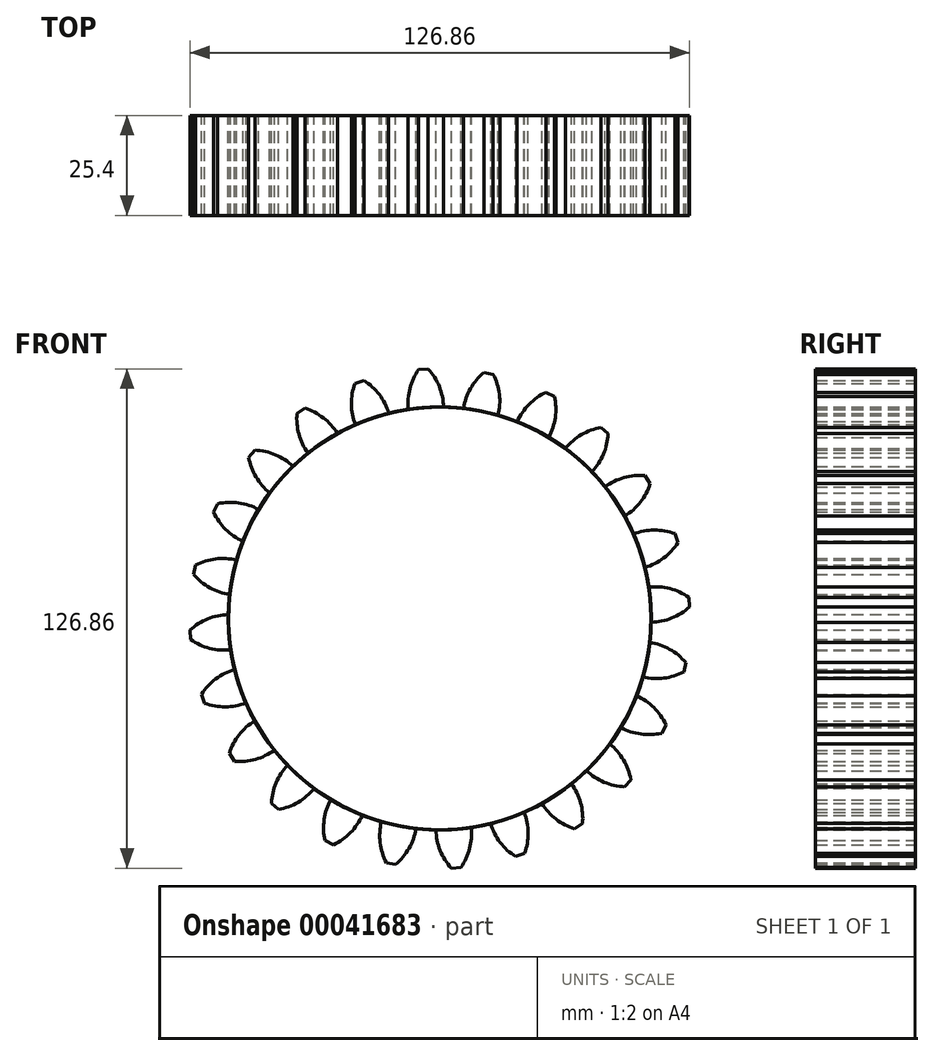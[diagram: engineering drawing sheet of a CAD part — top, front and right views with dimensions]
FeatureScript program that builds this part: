
annotation { "Feature Type Name" : "Feature", "Feature Type Description" : "" }
export const myFeature = defineFeature(function(context is Context, id is Id, definition is map)
    precondition{}
    {
        {
            var Q0;
            Q0=qCreatedBy(makeId("Front.planeOp"),FACE);
            var sketch = newSketch(context, id + "F0", { "sketchPlane" : qUnion([Q0])});
            skCircle(sketch, "E0", {"center": v(0, 0) * mm, "radius": 53.72 * mm});
            skCircle(sketch, "E1", {"center": v(0, 0) * mm, "radius": 58.67 * mm, "construction": true});
            skCircle(sketch, "E2", {"center": v(0, 0) * mm, "radius": 63.5 * mm, "construction": true});
            skLineSegment(sketch, "E3", {"start": v(0, 0) * mm, "end": v(0, 76.8) * mm, "construction": true});
            skLineSegment(sketch, "E4", {"start": v(0, 0) * mm, "end": v(-5.04, 76.92) * mm, "construction": true});
            skLineSegment(sketch, "E5", {"start": v(0, 58.67) * mm, "end": v(-86.24, 58.67) * mm, "construction": true});
            skLineSegment(sketch, "E6", {"start": v(0, 58.67) * mm, "end": v(-90.6, 25.7) * mm, "construction": true});
            skCircle(sketch, "E7", {"center": v(0, 58.67) * mm, "radius": 14.6 * mm, "construction": true});
            skCircle(sketch, "E8", {"center": v(0, 0) * mm, "radius": 55.14 * mm, "construction": true});
            skCircle(sketch, "E9", {"center": v(-13.63, 53.42) * mm, "radius": 14.6 * mm, "construction": true});
            skArc(sketch, "E10", {"start": v(0, 58.63) * mm, "mid": v(0, 58.65) * mm, "end": v(-0.02, 58.67) * mm});
            skPoint(sketch, "E11.orphan", {"position": v(-5.32, 63.28) * mm});
            skPoint(sketch, "E12.MirrorCS.start.orphan", {"position": v(-7.98, 53.13) * mm});
            skPoint(sketch, "E13.orphan", {"position": v(0.97, 53.71) * mm});
            skPoint(sketch, "E14.orphan", {"position": v(-2.99, 63.43) * mm});
            skArc(sketch, "E15", {"start": v(0.97, 53.67) * mm, "mid": v(-0.1, 58.91) * mm, "end": v(-2.96, 63.43) * mm});
            skArc(sketch, "E16.MirrorCS", {"start": v(-7.97, 53.09) * mm, "mid": v(-7.59, 58.42) * mm, "end": v(-5.35, 63.27) * mm});
            skLineSegment(sketch, "E17", {"start": v(-5.35, 63.27) * mm, "end": v(-2.96, 63.43) * mm});
            skSolve(sketch);
        }
        {
            var Q0;
            {var subQ0=sQuery(id+"F0.wireOp",EDGE,"E17");Q0=makeQuery(id+"F0.imprint","IMPRINT",FACE,{"disambiguationData":[TD([[makeQuery(id+"F0.imprint","IMPRINT",EDGE,{"derivedFrom":subQ0}),-1.0]])]});}
            var Q1;
            {var subQ0=sQuery(id+"F0.wireOp",EDGE,"E0");var subQ2=makeQuery(id+"F0.imprint","INTERSECT",VERTEX,{"derivedFrom":[subQ0,sQuery(id+"F0.wireOp",EDGE,"E15")]});Q1=makeQuery(id+"F0.imprint","IMPRINT",FACE,{"disambiguationData":[TD([[makeQuery(id+"F0.imprint","IMPRINT",EDGE,{"disambiguationData":[TD([[subQ2,-1.0]])],"derivedFrom":subQ0}),1.0]])]});}
            extrude(context, id + "F1", {"entities" : qUnion([Q0, Q1]), "depth" : 25.4 * mm});
        }
        {
            var Q0;
            Q0=makeQuery(id+"F1.opExtrude","SWEPT_BODY",BODY,{"disambiguationData":[OSD([sQuery(id+"F0.wireOp",EDGE,"E0"),sQuery(id+"F0.wireOp",EDGE,"E15"),sQuery(id+"F0.wireOp",EDGE,"E16.MirrorCS"),sQuery(id+"F0.wireOp",EDGE,"E17")])]});
            var Q1;
            Q1=makeQuery(id+"F1.opExtrude","SWEPT_FACE",FACE,{"disambiguationData":[OSD([sQuery(id+"F0.wireOp",EDGE,"E0")])]});
            circularPattern(context, id + "F2", {"entities" : qUnion([Q0]), "axis" : qUnion([Q1]), "angle" : 15 * degree, "instanceCount" : round(24)});
        }
    });
